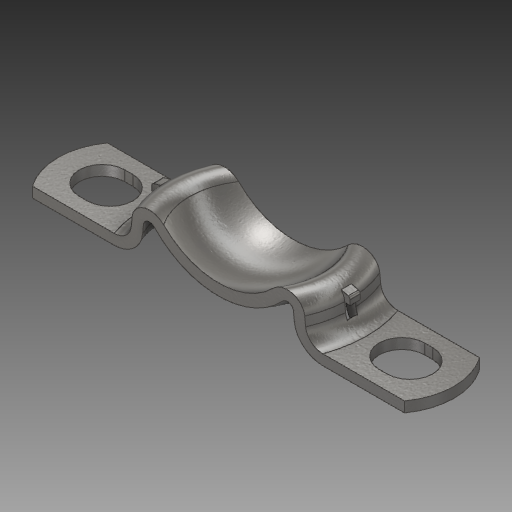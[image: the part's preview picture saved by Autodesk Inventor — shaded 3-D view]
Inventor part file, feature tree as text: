
AUTODESK INVENTOR PART (.ipt)
format: ipt  version: 2017.1 (Build 211199000, 199)  size: 290,304 bytes
history: native  units: in
note: dims shown in document units (in); Inventor stores cm internally (conversion verified against a paired STEP export)
features: mirror x1
ambient origin geometry x8: Origin, YZ Plane, XZ Plane, XY Plane, X Axis, Y Axis, Z Axis, Center Point
bodies: Solid1 (feature_tree)
feature tree (1):
  mirror  "Mirror1"
